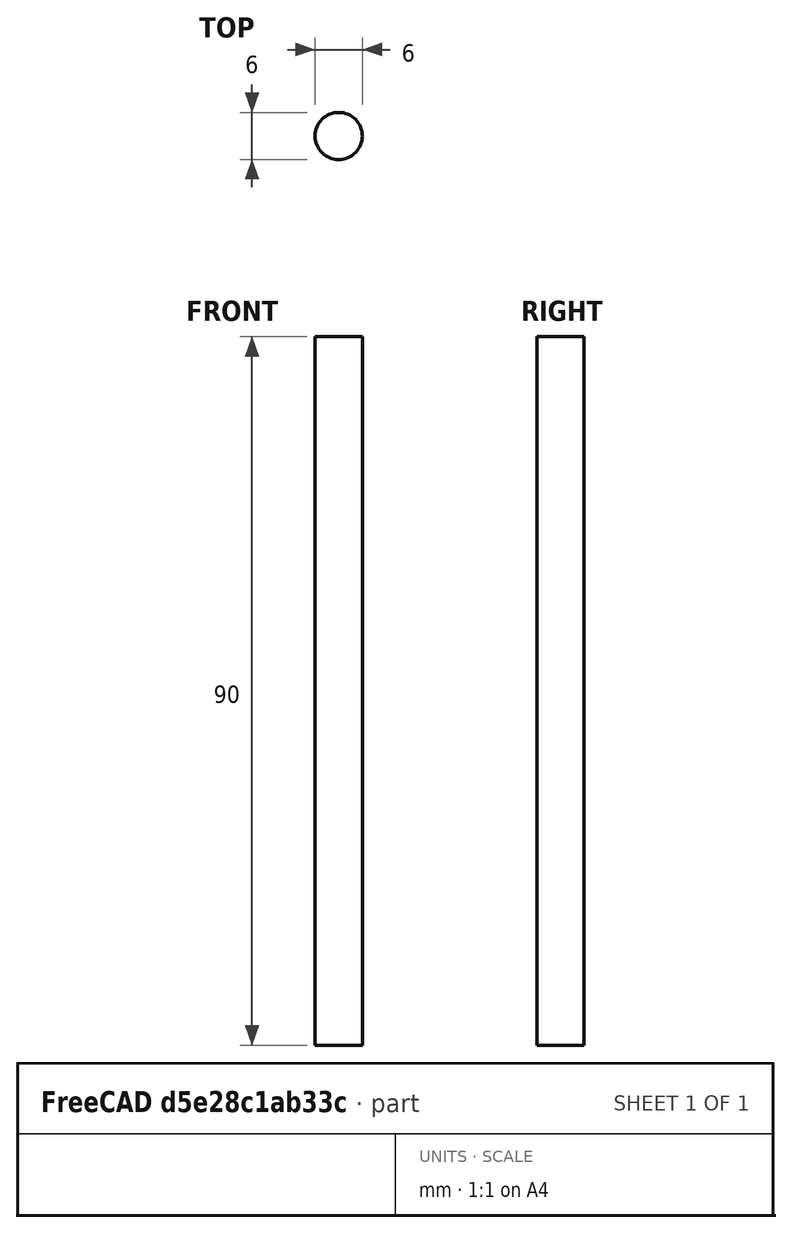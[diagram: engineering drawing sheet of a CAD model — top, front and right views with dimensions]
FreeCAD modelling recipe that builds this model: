
FCSTD DOCUMENT  (FreeCAD 2022.709R28846 (Git))
Label: fischband_pin
License: All rights reserved
LicenseURL: http://en.wikipedia.org/wiki/All_rights_reserved
objects: Sketcher::SketchObject×1, PartDesign::Pad×1, PartDesign::Body×1
note: 5 computed .brp shape members not serialized (recipe doc carries the construction recipe); baked Part::Feature solids carry a one-line shape summary decoded from their .brp

FEATURE [Sketcher::SketchObject] Sketch
  ArcFitTolerance = 1e-06
  AttachmentSupport = -> [XY_Plane]
  FullyConstrained = true
  MapMode = 5
  Support = -> [XY_Plane]
  TreeRank = 13
  sketch-geometry (1):
    g0: Circle CenterX=0 CenterY=0 CenterZ=0 NormalX=0 NormalY=0 NormalZ=1 AngleXU=0 Radius=3
  constraints (2):
    c: Coincident(g0,g-1)
    c: Radius(g0) = 3
FEATURE [PartDesign::Pad] Pad
  ClaimChildren = false
  Direction = (0,0,1)
  Fit = 0
  FitJoin = 0
  InnerFit = 0
  InnerFitJoin = 0
  InnerTaperAngle = 0
  InnerTaperAngleRev = 0
  Length = 90
  Length2 = 100
  Linearize = true
  NewSolid = false
  Profile = -> Sketch
  Suppress = false
  TreeRank = 14
  Type = 0
  _ProfileBasedVersion = 1
FEATURE [PartDesign::Body] Body
  AutoGroupSolids = false
  ClaimAllChildren = false
  ExportMode = 0
  Group = -> [Sketch,Pad]
  Origin = -> Origin
  Tip = -> Pad
  TreeRank = 12
  _ExportChildren = -> [Pad]
  _GroupVersion = 1
